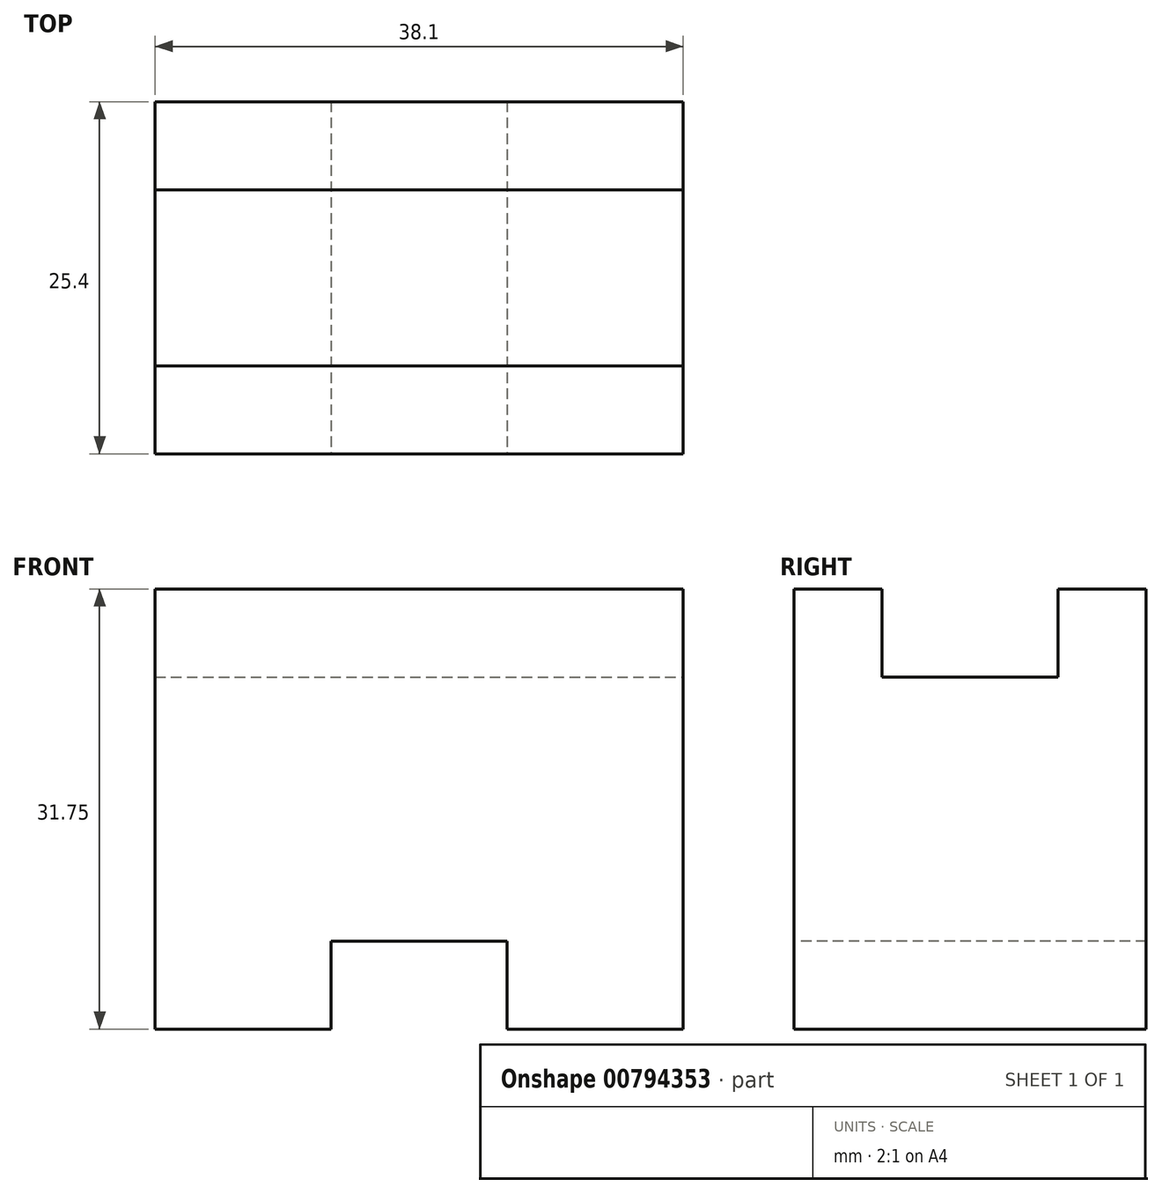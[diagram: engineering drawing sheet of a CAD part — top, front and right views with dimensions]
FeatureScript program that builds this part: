
annotation { "Feature Type Name" : "Feature", "Feature Type Description" : "" }
export const myFeature = defineFeature(function(context is Context, id is Id, definition is map)
    precondition{}
    {
        {
            var Q0;
            Q0=qCreatedBy(makeId("Right.planeOp"),FACE);
            var sketch = newSketch(context, id + "F0", { "sketchPlane" : qUnion([Q0])});
            skLineSegment(sketch, "E0", {"start": v(0, 0) * mm, "end": v(25.4, 0) * mm});
            skLineSegment(sketch, "E1", {"start": v(25.4, 0) * mm, "end": v(25.4, 31.75) * mm});
            skLineSegment(sketch, "E2", {"start": v(25.4, 31.75) * mm, "end": v(0, 31.75) * mm});
            skLineSegment(sketch, "E3", {"start": v(0, 31.75) * mm, "end": v(0, 0) * mm});
            skSolve(sketch);
        }
        {
            var Q0;
            Q0 = qSketchRegion(id + "F0", true);
            extrude(context, id + "F1", {"entities" : qUnion([Q0]), "depth" : 38.1 * mm, "offsetDistance" : 25.4 * mm});
        }
        {
            var Q0;
            Q0=makeQuery(id+"F1.opExtrude","CAP_FACE",FACE,{"disambiguationData":[OSD([sQuery(id+"F0.wireOp",EDGE,"E0"),sQuery(id+"F0.wireOp",EDGE,"E1"),sQuery(id+"F0.wireOp",EDGE,"E2"),sQuery(id+"F0.wireOp",EDGE,"E3")])],"isStart":false});
            var sketch = newSketch(context, id + "F2", { "sketchPlane" : qUnion([Q0])});
            skLineSegment(sketch, "E4", {"start": v(0, 31.75) * mm, "end": v(6.35, 31.75) * mm, "construction": true});
            skLineSegment(sketch, "E5", {"start": v(6.35, 31.75) * mm, "end": v(6.35, 25.4) * mm});
            skLineSegment(sketch, "E6", {"start": v(6.35, 25.4) * mm, "end": v(19.05, 25.4) * mm});
            skLineSegment(sketch, "E7", {"start": v(19.05, 25.4) * mm, "end": v(19.05, 31.75) * mm});
            skSolve(sketch);
        }
        {
            var Q0;
            Q0 = qSketchRegion(id + "F2", true);
            var Q1;
            {var subQ0=sQuery(id+"F2.wireOp",EDGE,"E5");Q1=makeQuery(id+"F2.imprint","IMPRINT",FACE,{"disambiguationData":[TD([[makeQuery(id+"F2.imprint","IMPRINT",EDGE,{"derivedFrom":subQ0}),1.0]])]});}
            extrude(context, id + "F3", {"entities" : qUnion([Q0, Q1]), "operationType" : NewBodyOperationType.REMOVE, "oppositeDirection" : true, "depth" : 50.8 * mm, "offsetDistance" : 25.4 * mm});
        }
        {
            var Q0;
            Q0=makeQuery(id+"F1.opExtrude","SWEPT_FACE",FACE,{"disambiguationData":[OSD([sQuery(id+"F0.wireOp",EDGE,"E3")])]});
            var sketch = newSketch(context, id + "F4", { "sketchPlane" : qUnion([Q0])});
            skLineSegment(sketch, "E8", {"start": v(0, 0) * mm, "end": v(12.7, 0) * mm, "construction": true});
            skLineSegment(sketch, "E9", {"start": v(12.7, 0) * mm, "end": v(12.7, 6.35) * mm});
            skLineSegment(sketch, "E10", {"start": v(12.7, 6.35) * mm, "end": v(25.4, 6.35) * mm});
            skLineSegment(sketch, "E11", {"start": v(25.4, 6.35) * mm, "end": v(25.4, 0) * mm});
            skSolve(sketch);
        }
        {
            var Q0;
            Q0 = qSketchRegion(id + "F4", true);
            var Q1;
            {var subQ0=sQuery(id+"F4.wireOp",EDGE,"E9");Q1=makeQuery(id+"F4.imprint","IMPRINT",FACE,{"disambiguationData":[TD([[makeQuery(id+"F4.imprint","IMPRINT",EDGE,{"derivedFrom":subQ0}),-1.0]])]});}
            extrude(context, id + "F5", {"entities" : qUnion([Q0, Q1]), "operationType" : NewBodyOperationType.REMOVE, "oppositeDirection" : true, "depth" : 50.8 * mm, "offsetDistance" : 25.4 * mm});
        }
    });
